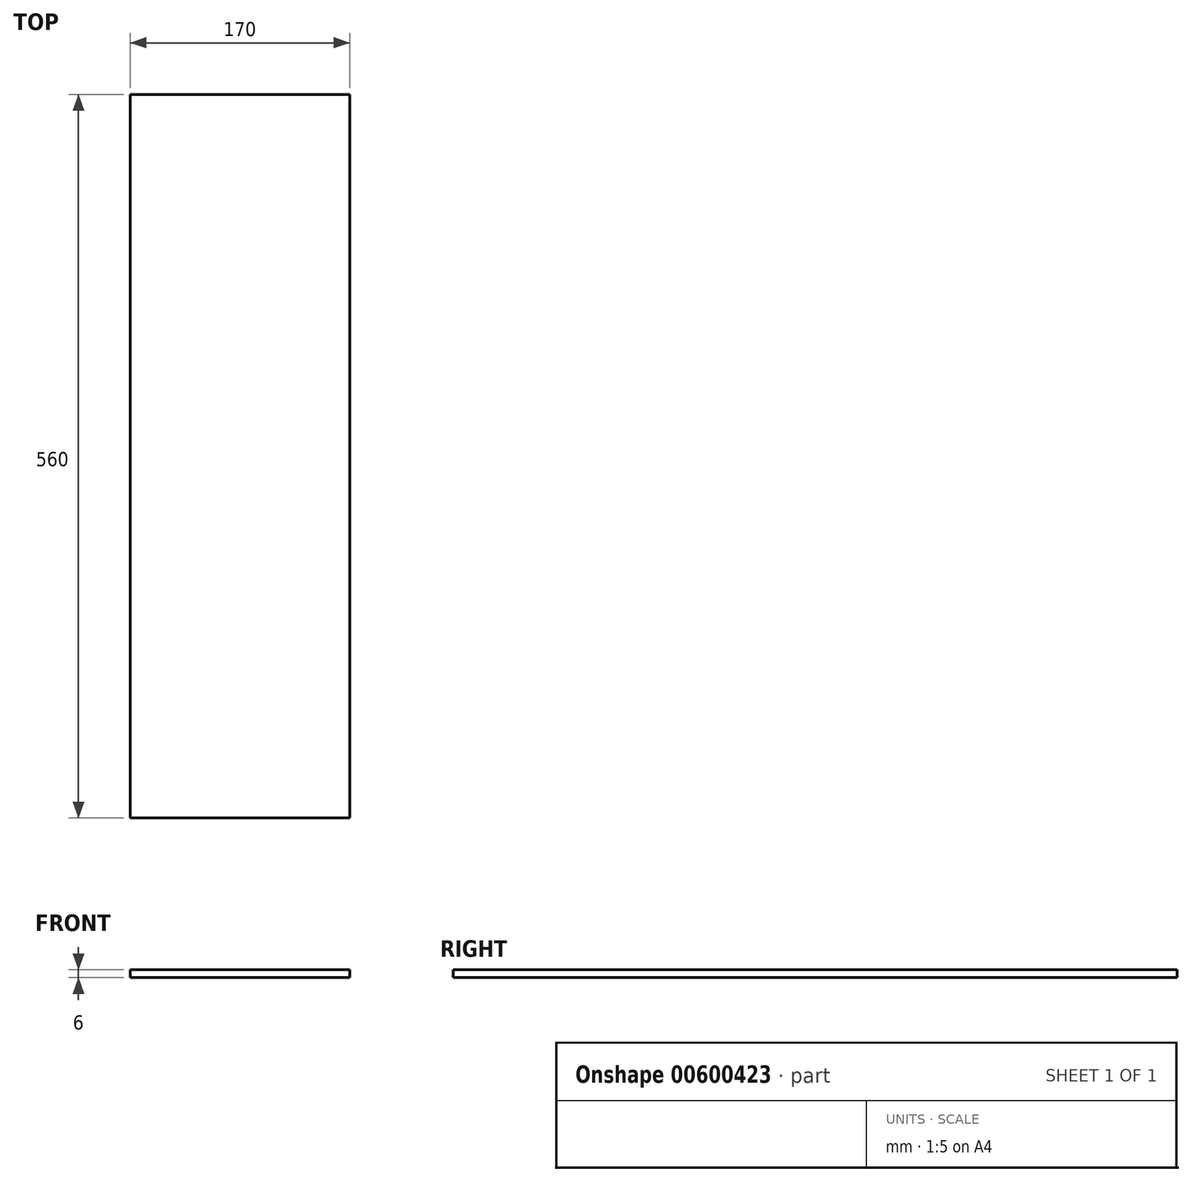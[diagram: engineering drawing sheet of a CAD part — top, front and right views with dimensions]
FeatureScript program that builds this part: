
annotation { "Feature Type Name" : "Feature", "Feature Type Description" : "" }
export const myFeature = defineFeature(function(context is Context, id is Id, definition is map)
    precondition{}
    {
        {
            var Q0;
            Q0=qCreatedBy(makeId("Top.planeOp"),FACE);
            var sketch = newSketch(context, id + "F0", { "sketchPlane" : qUnion([Q0])});
            skLineSegment(sketch, "E0.bottom", {"start": v(-198.06, -281.93) * mm, "end": v(-28.06, -281.93) * mm});
            skLineSegment(sketch, "E0.top", {"start": v(-198.06, 278.07) * mm, "end": v(-28.06, 278.07) * mm});
            skLineSegment(sketch, "E0.left", {"start": v(-198.06, -281.93) * mm, "end": v(-198.06, 278.07) * mm});
            skLineSegment(sketch, "E0.right", {"start": v(-28.06, -281.93) * mm, "end": v(-28.06, 278.07) * mm});
            skSolve(sketch);
        }
        {
            var Q0;
            Q0 = qSketchRegion(id + "F0", true);
            extrude(context, id + "F1", {"entities" : qUnion([Q0]), "depth" : 6 * mm, "offsetDistance" : 25 * mm});
        }
    });
